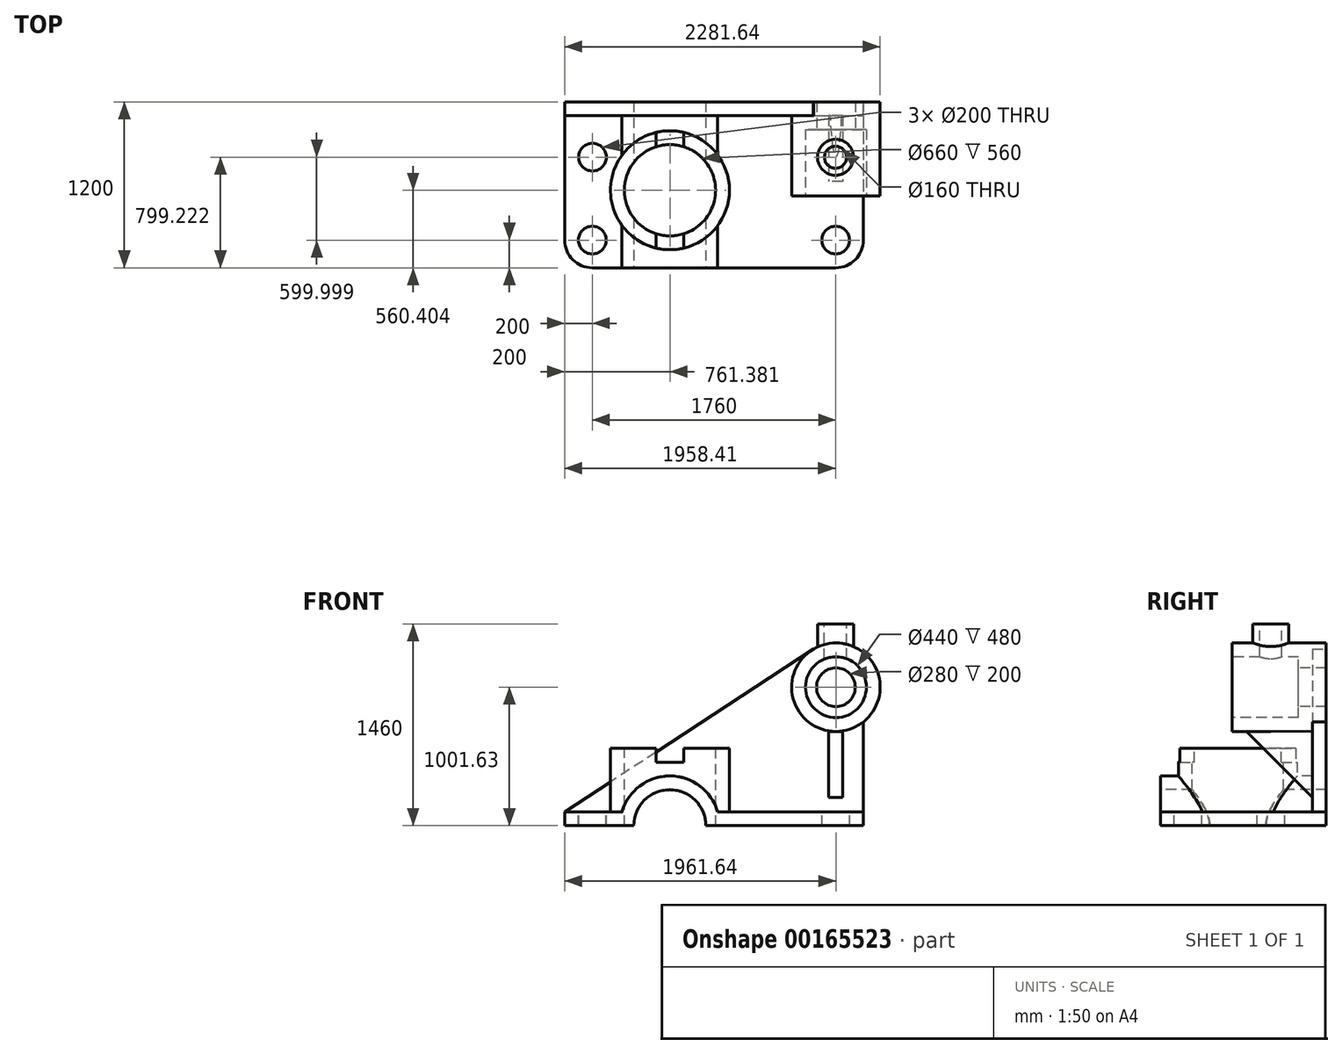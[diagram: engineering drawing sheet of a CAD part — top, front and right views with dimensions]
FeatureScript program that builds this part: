
annotation { "Feature Type Name" : "Feature", "Feature Type Description" : "" }
export const myFeature = defineFeature(function(context is Context, id is Id, definition is map)
    precondition{}
    {
        {
            var Q0;
            Q0=qCreatedBy(makeId("Top.planeOp"),FACE);
            var sketch = newSketch(context, id + "F0", { "sketchPlane" : qUnion([Q0])});
            skLineSegment(sketch, "E0.bottom", {"start": v(1080, 600) * mm, "end": v(-1080, 600) * mm});
            skLineSegment(sketch, "E0.top", {"start": v(1080, -600) * mm, "end": v(-1080, -600) * mm});
            skLineSegment(sketch, "E0.left", {"start": v(1080, 600) * mm, "end": v(1080, -600) * mm});
            skLineSegment(sketch, "E0.right", {"start": v(-1080, 600) * mm, "end": v(-1080, -600) * mm});
            skPoint(sketch, "E0.middle", {"position": v(0, 0) * mm});
            skSolve(sketch);
        }
        {
            var Q0;
            Q0 = qSketchRegion(id + "F0", true);
            extrude(context, id + "F1", {"entities" : qUnion([Q0]), "depth" : 100 * mm});
        }
        {
            var Q0;
            Q0=makeQuery(id+"F1.opExtrude","SWEPT_EDGE",EDGE,{"disambiguationData":[OSD([sQuery(id+"F0.wireOp",EDGE,"E0.top"),sQuery(id+"F0.wireOp",EDGE,"E0.right")])]});
            fillet(context, id + "F2", {"entities" : qUnion([Q0]), "radius" : 200 * mm, "tangentPropagation" : true, "allowEdgeOverflow" : false});
        }
        {
            var Q0;
            Q0=makeQuery(id+"F1.opExtrude","SWEPT_EDGE",EDGE,{"disambiguationData":[OSD([sQuery(id+"F0.wireOp",EDGE,"E0.top"),sQuery(id+"F0.wireOp",EDGE,"E0.left")])]});
            fillet(context, id + "F3", {"entities" : qUnion([Q0]), "radius" : 200 * mm, "tangentPropagation" : true, "allowEdgeOverflow" : false});
        }
        {
            var Q0;
            Q0=makeQuery(id+"F1.opExtrude","CAP_FACE",FACE,{"disambiguationData":[OSD([sQuery(id+"F0.wireOp",EDGE,"E0.bottom"),sQuery(id+"F0.wireOp",EDGE,"E0.top"),sQuery(id+"F0.wireOp",EDGE,"E0.left"),sQuery(id+"F0.wireOp",EDGE,"E0.right")])],"isStart":false});
            var sketch = newSketch(context, id + "F4", { "sketchPlane" : qUnion([Q0])});
            skCircle(sketch, "E1", {"center": v(-878.76, 200) * mm, "radius": 100 * mm});
            skCircle(sketch, "E2", {"center": v(-880, -400) * mm, "radius": 100 * mm});
            skLineSegment(sketch, "E3", {"start": v(-880, -400) * mm, "end": v(880, -400) * mm});
            skCircle(sketch, "E4", {"center": v(880, -400) * mm, "radius": 100 * mm});
            skLineSegment(sketch, "E5", {"start": v(-880, -400) * mm, "end": v(-878.76, 200) * mm});
            skLineSegment(sketch, "E6", {"start": v(-880, -400) * mm, "end": v(-880, -600) * mm});
            skLineSegment(sketch, "E7", {"start": v(-880, -400) * mm, "end": v(-1080, -400) * mm});
            skLineSegment(sketch, "E8", {"start": v(880, -400) * mm, "end": v(880, -600) * mm});
            skLineSegment(sketch, "E9", {"start": v(880, -400) * mm, "end": v(1080, -400) * mm});
            skSolve(sketch);
        }
        {
            var Q0;
            {var subQ0=sQuery(id+"F4.wireOp",EDGE,"E9");var subQ1=sQuery(id+"F4.wireOp",EDGE,"E4");var subQ2=makeQuery(id+"F4.imprint","INTERSECT",VERTEX,{"derivedFrom":[subQ1,subQ0]});Q0=makeQuery(id+"F4.imprint","IMPRINT",FACE,{"disambiguationData":[TD([[makeQuery(id+"F4.imprint","IMPRINT",EDGE,{"disambiguationData":[TD([[subQ2,1.0]])],"derivedFrom":subQ1}),1.0]])]});}
            var Q1;
            {var subQ1=sQuery(id+"F4.wireOp",EDGE,"E3");var subQ3=sQuery(id+"F4.wireOp",EDGE,"E4");var subQ4=makeQuery(id+"F4.imprint","INTERSECT",VERTEX,{"derivedFrom":[subQ1,subQ3]});Q1=makeQuery(id+"F4.imprint","IMPRINT",FACE,{"disambiguationData":[TD([[makeQuery(id+"F4.imprint","IMPRINT",EDGE,{"disambiguationData":[TD([[subQ4,1.0]])],"derivedFrom":subQ3}),1.0]])]});}
            var Q2;
            {var subQ1=sQuery(id+"F4.wireOp",EDGE,"E3");var subQ3=sQuery(id+"F4.wireOp",EDGE,"E4");var subQ4=makeQuery(id+"F4.imprint","INTERSECT",VERTEX,{"derivedFrom":[subQ1,subQ3]});Q2=makeQuery(id+"F4.imprint","IMPRINT",FACE,{"disambiguationData":[TD([[makeQuery(id+"F4.imprint","IMPRINT",EDGE,{"disambiguationData":[TD([[subQ4,-1.0]])],"derivedFrom":subQ3}),1.0]])]});}
            var Q3;
            {var subQ0=sQuery(id+"F4.wireOp",EDGE,"E5");var subQ1=sQuery(id+"F4.wireOp",EDGE,"E2");var subQ2=makeQuery(id+"F4.imprint","INTERSECT",VERTEX,{"derivedFrom":[subQ1,subQ0]});Q3=makeQuery(id+"F4.imprint","IMPRINT",FACE,{"disambiguationData":[TD([[makeQuery(id+"F4.imprint","IMPRINT",EDGE,{"disambiguationData":[TD([[subQ2,-1.0]])],"derivedFrom":subQ1}),1.0]])]});}
            var Q4;
            {var subQ0=sQuery(id+"F4.wireOp",EDGE,"E5");var subQ1=sQuery(id+"F4.wireOp",EDGE,"E2");var subQ2=makeQuery(id+"F4.imprint","INTERSECT",VERTEX,{"derivedFrom":[subQ1,subQ0]});Q4=makeQuery(id+"F4.imprint","IMPRINT",FACE,{"disambiguationData":[TD([[makeQuery(id+"F4.imprint","IMPRINT",EDGE,{"disambiguationData":[TD([[subQ2,1.0]])],"derivedFrom":subQ1}),1.0]])]});}
            var Q5;
            {var subQ0=sQuery(id+"F4.wireOp",EDGE,"E3");var subQ1=sQuery(id+"F4.wireOp",EDGE,"E2");var subQ2=makeQuery(id+"F4.imprint","INTERSECT",VERTEX,{"derivedFrom":[subQ1,subQ0]});Q5=makeQuery(id+"F4.imprint","IMPRINT",FACE,{"disambiguationData":[TD([[makeQuery(id+"F4.imprint","IMPRINT",EDGE,{"disambiguationData":[TD([[subQ2,1.0]])],"derivedFrom":subQ1}),1.0]])]});}
            var Q6;
            {var subQ0=sQuery(id+"F4.wireOp",EDGE,"E7");var subQ1=sQuery(id+"F4.wireOp",EDGE,"E2");var subQ2=makeQuery(id+"F4.imprint","INTERSECT",VERTEX,{"derivedFrom":[subQ1,subQ0]});Q6=makeQuery(id+"F4.imprint","IMPRINT",FACE,{"disambiguationData":[TD([[makeQuery(id+"F4.imprint","IMPRINT",EDGE,{"disambiguationData":[TD([[subQ2,-1.0]])],"derivedFrom":subQ1}),1.0]])]});}
            var Q7;
            Q7=makeQuery(id+"F4.imprint","IMPRINT",FACE,{"disambiguationData":[TD([[makeQuery(id+"F4.imprint","IMPRINT",EDGE,{"derivedFrom":sQuery(id+"F4.wireOp",EDGE,"E1")}),1.0]])]});
            extrude(context, id + "F5", {"entities" : qUnion([Q0, Q1, Q2, Q3, Q4, Q5, Q6, Q7]), "operationType" : NewBodyOperationType.REMOVE, "oppositeDirection" : true, "depth" : 100 * mm});
        }
        {
            var Q0;
            Q0=makeQuery(id+"F1.opExtrude","CAP_FACE",FACE,{"disambiguationData":[OSD([sQuery(id+"F0.wireOp",EDGE,"E0.bottom"),sQuery(id+"F0.wireOp",EDGE,"E0.top"),sQuery(id+"F0.wireOp",EDGE,"E0.left"),sQuery(id+"F0.wireOp",EDGE,"E0.right")])],"isStart":false});
            var sketch = newSketch(context, id + "F6", { "sketchPlane" : qUnion([Q0])});
            skCircle(sketch, "E10", {"center": v(-318.62, -39.6) * mm, "radius": 430 * mm});
            skSolve(sketch);
        }
        {
            var Q0;
            Q0 = qSketchRegion(id + "F6", true);
            extrude(context, id + "F7", {"entities" : qUnion([Q0]), "operationType" : NewBodyOperationType.ADD, "depth" : 460 * mm});
        }
        {
            var Q0;
            Q0=makeQuery(id+"F7.opExtrude","CAP_FACE",FACE,{"disambiguationData":[OSD([sQuery(id+"F6.wireOp",EDGE,"E10")])],"isStart":false});
            var sketch = newSketch(context, id + "F8", { "sketchPlane" : qUnion([Q0])});
            skLineSegment(sketch, "E11", {"start": v(-318.62, -39.6) * mm, "end": v(-418.62, -39.6) * mm});
            skLineSegment(sketch, "E12", {"start": v(-318.62, -39.6) * mm, "end": v(-218.62, -39.6) * mm});
            skLineSegment(sketch, "E13", {"start": v(-218.62, -39.6) * mm, "end": v(-218.62, 463.28) * mm});
            skLineSegment(sketch, "E14", {"start": v(-218.62, -39.6) * mm, "end": v(-218.62, -515.68) * mm});
            skLineSegment(sketch, "E15", {"start": v(-418.62, -39.6) * mm, "end": v(-418.62, 463.28) * mm});
            skLineSegment(sketch, "E16", {"start": v(-418.62, -39.6) * mm, "end": v(-418.62, -515.68) * mm});
            skLineSegment(sketch, "E17", {"start": v(-418.62, -515.68) * mm, "end": v(-218.62, -515.68) * mm});
            skLineSegment(sketch, "E18", {"start": v(-218.62, 463.28) * mm, "end": v(-418.62, 463.28) * mm});
            skLineSegment(sketch, "E19", {"start": v(-318.62, -39.6) * mm, "end": v(-318.62, -515.68) * mm});
            skSolve(sketch);
        }
        {
            var Q0;
            Q0 = qSketchRegion(id + "F8", true);
            extrude(context, id + "F9", {"entities" : qUnion([Q0]), "operationType" : NewBodyOperationType.REMOVE, "oppositeDirection" : true, "depth" : 100 * mm});
        }
        {
            var Q0;
            Q0=qCreatedBy(makeId("Front.planeOp"),FACE);
            cPlane(context, id + "F10", {"entities" : qUnion([Q0]), "cplaneType" : CPlaneType.OFFSET, "offset" : 600 * mm, "width" : 150 * mm, "height" : 150 * mm});
        }
        {
            var Q0;
            Q0=qCreatedBy(id+"F10.planeOp",FACE);
            var sketch = newSketch(context, id + "F11", { "sketchPlane" : qUnion([Q0])});
            skLineSegment(sketch, "E20", {"start": v(-319.41, 550.92) * mm, "end": v(-319.41, 0) * mm});
            skCircle(sketch, "E21", {"center": v(-319.41, 0) * mm, "radius": 260 * mm});
            skCircle(sketch, "E22", {"center": v(-319.41, 0) * mm, "radius": 360 * mm});
            skSolve(sketch);
        }
        {
            var Q0;
            Q0=makeQuery(id+"F11.imprint","IMPRINT",FACE,{"disambiguationData":[TD([[makeQuery(id+"F11.imprint","IMPRINT",EDGE,{"derivedFrom":sQuery(id+"F11.wireOp",EDGE,"E21")}),-1.0]])]});
            extrude(context, id + "F12", {"entities" : qUnion([Q0]), "operationType" : NewBodyOperationType.ADD, "oppositeDirection" : true, "depth" : 1200 * mm});
        }
        {
            var Q0;
            Q0=makeQuery(id+"F11.imprint","IMPRINT",FACE,{"disambiguationData":[TD([[makeQuery(id+"F11.imprint","IMPRINT",EDGE,{"derivedFrom":sQuery(id+"F11.wireOp",EDGE,"E21")}),-1.0]])]});
            var sketch = newSketch(context, id + "F13", { "sketchPlane" : qUnion([Q0])});
            skLineSegment(sketch, "E23.bottom", {"start": v(53.56, 0) * mm, "end": v(-696.44, 0) * mm});
            skLineSegment(sketch, "E23.top", {"start": v(53.56, -370) * mm, "end": v(-696.44, -370) * mm});
            skLineSegment(sketch, "E23.left", {"start": v(53.56, 0) * mm, "end": v(53.56, -370) * mm});
            skLineSegment(sketch, "E23.right", {"start": v(-696.44, 0) * mm, "end": v(-696.44, -370) * mm});
            skPoint(sketch, "E23.middle", {"position": v(-321.44, -185) * mm});
            skSolve(sketch);
        }
        {
            var Q0;
            Q0 = qSketchRegion(id + "F13", true);
            extrude(context, id + "F14", {"entities" : qUnion([Q0]), "operationType" : NewBodyOperationType.REMOVE, "endBound" : BoundingType.THROUGH_ALL, "oppositeDirection" : true, "depth" : 25 * mm});
        }
        {
            var Q0;
            Q0=makeQuery(id+"F7.opExtrude","CAP_FACE",FACE,{"disambiguationData":[OSD([sQuery(id+"F6.wireOp",EDGE,"E10")])],"isStart":false});
            var sketch = newSketch(context, id + "F15", { "sketchPlane" : qUnion([Q0])});
            skCircle(sketch, "E24", {"center": v(-318.62, -39.6) * mm, "radius": 330 * mm});
            skSolve(sketch);
        }
        {
            var Q0;
            Q0 = qSketchRegion(id + "F15", true);
            extrude(context, id + "F16", {"entities" : qUnion([Q0]), "operationType" : NewBodyOperationType.REMOVE, "oppositeDirection" : true, "depth" : 560 * mm});
        }
        {
            var Q0;
            Q0=qCreatedBy(id+"F10.planeOp",FACE);
            cPlane(context, id + "F17", {"entities" : qUnion([Q0]), "cplaneType" : CPlaneType.OFFSET, "offset" : 1200 * mm, "oppositeDirection" : true, "width" : 150 * mm, "height" : 150 * mm});
        }
        {
            var Q0;
            Q0=qCreatedBy(id+"F17.planeOp",FACE);
            var sketch = newSketch(context, id + "F18", { "sketchPlane" : qUnion([Q0])});
            skCircle(sketch, "E25", {"center": v(881.64, 1001.63) * mm, "radius": 320 * mm});
            skSolve(sketch);
        }
        {
            var Q0;
            Q0=qCreatedBy(id+"F17.planeOp",FACE);
            var sketch = newSketch(context, id + "F19", { "sketchPlane" : qUnion([Q0])});
            skLineSegment(sketch, "E26", {"start": v(719.16, 1278.32) * mm, "end": v(-1078.96, 99.5) * mm});
            skLineSegment(sketch, "E27", {"start": v(-1078.96, 99.5) * mm, "end": v(1080.94, 99.5) * mm});
            skLineSegment(sketch, "E28", {"start": v(1080.94, 99.5) * mm, "end": v(1080.94, 752.38) * mm});
            skLineSegment(sketch, "E29", {"start": v(1080.94, 752.38) * mm, "end": v(719.16, 1278.32) * mm});
            skSolve(sketch);
        }
        {
            var Q0;
            Q0 = qSketchRegion(id + "F19", true);
            extrude(context, id + "F20", {"entities" : qUnion([Q0]), "operationType" : NewBodyOperationType.ADD, "depth" : 100 * mm});
        }
        {
            var Q0;
            Q0=makeQuery(id+"F11.imprint","IMPRINT",FACE,{"disambiguationData":[TD([[makeQuery(id+"F11.imprint","IMPRINT",EDGE,{"derivedFrom":sQuery(id+"F11.wireOp",EDGE,"E21")}),1.0]])]});
            extrude(context, id + "F21", {"entities" : qUnion([Q0]), "operationType" : NewBodyOperationType.REMOVE, "endBound" : BoundingType.THROUGH_ALL, "oppositeDirection" : true, "depth" : 25 * mm});
        }
        {
            var Q0;
            Q0 = qSketchRegion(id + "F18", true);
            extrude(context, id + "F22", {"entities" : qUnion([Q0]), "operationType" : NewBodyOperationType.ADD, "depth" : 680 * mm});
        }
        {
            var Q0;
            Q0=makeQuery(id+"F22.opExtrude","CAP_FACE",FACE,{"disambiguationData":[OSD([sQuery(id+"F18.wireOp",EDGE,"E25")])],"isStart":false});
            var sketch = newSketch(context, id + "F23", { "sketchPlane" : qUnion([Q0])});
            skCircle(sketch, "E30", {"center": v(881.64, 1001.63) * mm, "radius": 220 * mm});
            skSolve(sketch);
        }
        {
            var Q0;
            Q0 = qSketchRegion(id + "F23", true);
            extrude(context, id + "F24", {"entities" : qUnion([Q0]), "operationType" : NewBodyOperationType.REMOVE, "oppositeDirection" : true, "depth" : 480 * mm});
        }
        {
            var Q0;
            Q0=qCreatedBy(makeId("Top.planeOp"),FACE);
            cPlane(context, id + "F25", {"entities" : qUnion([Q0]), "cplaneType" : CPlaneType.OFFSET, "offset" : 1460 * mm, "width" : 150 * mm, "height" : 150 * mm});
        }
        {
            var Q0;
            Q0=qCreatedBy(id+"F25.planeOp",FACE);
            var sketch = newSketch(context, id + "F26", { "sketchPlane" : qUnion([Q0])});
            skCircle(sketch, "E31", {"center": v(878.4, 199.22) * mm, "radius": 130 * mm});
            skSolve(sketch);
        }
        {
            var Q0;
            Q0 = qSketchRegion(id + "F26", true);
            extrude(context, id + "F27", {"entities" : qUnion([Q0]), "operationType" : NewBodyOperationType.ADD, "oppositeDirection" : true, "depth" : 170 * mm});
        }
        {
            var Q0;
            Q0=makeQuery(id+"F27.opExtrude","CAP_FACE",FACE,{"disambiguationData":[OSD([sQuery(id+"F26.wireOp",EDGE,"E31")])],"isStart":true});
            var sketch = newSketch(context, id + "F28", { "sketchPlane" : qUnion([Q0])});
            skCircle(sketch, "E32", {"center": v(878.4, 199.22) * mm, "radius": 80 * mm});
            skSolve(sketch);
        }
        {
            var Q0;
            Q0 = qSketchRegion(id + "F28", true);
            extrude(context, id + "F29", {"entities" : qUnion([Q0]), "operationType" : NewBodyOperationType.REMOVE, "oppositeDirection" : true, "depth" : 260 * mm});
        }
        {
            var Q0;
            Q0=makeQuery(id+"F24.boolean.opBoolean","COPY",FACE,{"derivedFrom":makeQuery(id+"F24.opExtrude","CAP_FACE",FACE,{"disambiguationData":[OSD([sQuery(id+"F23.wireOp",EDGE,"E30")])],"isStart":false})});
            var sketch = newSketch(context, id + "F30", { "sketchPlane" : qUnion([Q0])});
            skCircle(sketch, "E33", {"center": v(881.64, 1001.63) * mm, "radius": 140 * mm});
            skSolve(sketch);
        }
        {
            var Q0;
            Q0 = qSketchRegion(id + "F30", true);
            extrude(context, id + "F31", {"entities" : qUnion([Q0]), "operationType" : NewBodyOperationType.REMOVE, "endBound" : BoundingType.THROUGH_ALL, "oppositeDirection" : true, "depth" : 25 * mm});
        }
        {
            var Q0;
            Q0=makeQuery(id+"F1.opExtrude","SWEPT_FACE",FACE,{"disambiguationData":[OSD([sQuery(id+"F0.wireOp",EDGE,"E0.left")])]});
            cPlane(context, id + "F32", {"entities" : qUnion([Q0]), "cplaneType" : CPlaneType.OFFSET, "offset" : 200 * mm, "oppositeDirection" : true, "width" : 150 * mm, "height" : 150 * mm});
        }
        {
            var Q0;
            Q0=qCreatedBy(id+"F32.planeOp",FACE);
            var sketch = newSketch(context, id + "F33", { "sketchPlane" : qUnion([Q0])});
            skLineSegment(sketch, "E34", {"start": v(24.58, 680.12) * mm, "end": v(502.3, 200.79) * mm});
            skLineSegment(sketch, "E35", {"start": v(502.3, 200.79) * mm, "end": v(502.3, 684.25) * mm});
            skLineSegment(sketch, "E36", {"start": v(502.3, 684.25) * mm, "end": v(24.58, 680.12) * mm});
            skSolve(sketch);
        }
        {
            var Q0;
            Q0 = qSketchRegion(id + "F33", true);
            extrude(context, id + "F34", {"entities" : qUnion([Q0]), "operationType" : NewBodyOperationType.ADD, "depth" : 50 * mm});
        }
        {
            var Q0;
            Q0 = qSketchRegion(id + "F33", true);
            extrude(context, id + "F35", {"entities" : qUnion([Q0]), "operationType" : NewBodyOperationType.ADD, "oppositeDirection" : true, "depth" : 50 * mm});
        }
    });
